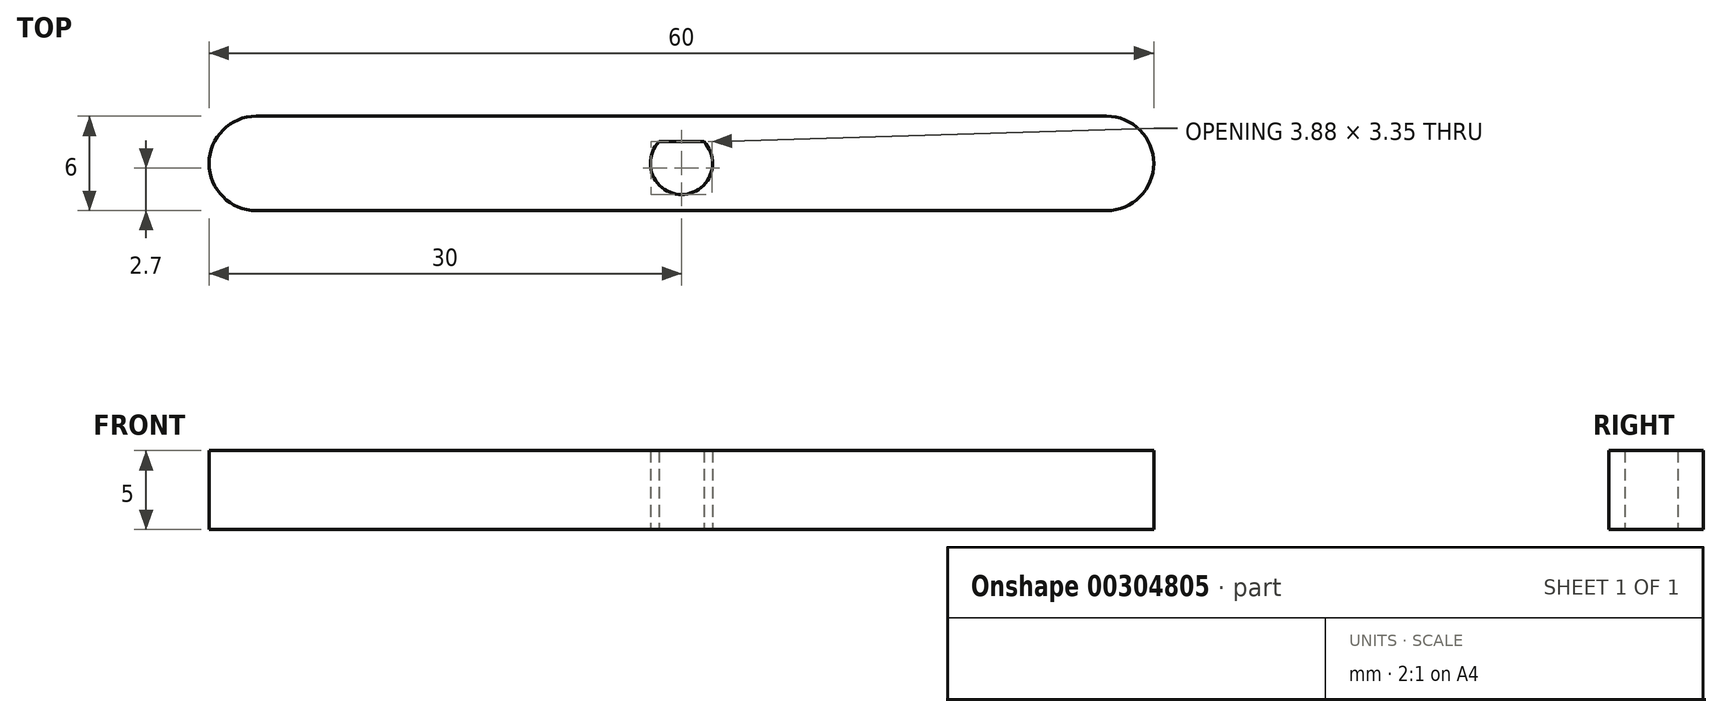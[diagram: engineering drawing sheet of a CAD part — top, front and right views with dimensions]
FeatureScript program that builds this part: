
annotation { "Feature Type Name" : "Feature", "Feature Type Description" : "" }
export const myFeature = defineFeature(function(context is Context, id is Id, definition is map)
    precondition{}
    {
        {
            var Q0;
            Q0=qCreatedBy(makeId("Top.planeOp"),FACE);
            var sketch = newSketch(context, id + "F0", { "sketchPlane" : qUnion([Q0])});
            skLineSegment(sketch, "E0.bottom", {"start": v(27, -3) * mm, "end": v(-27, -3) * mm});
            skLineSegment(sketch, "E0.top", {"start": v(27, 3) * mm, "end": v(-27, 3) * mm});
            skLineSegment(sketch, "E0.left", {"start": v(30, 0) * mm, "end": v(30, 0) * mm});
            skLineSegment(sketch, "E0.right", {"start": v(-30, 0) * mm, "end": v(-30, 0) * mm});
            skPoint(sketch, "E1.visualSharp", {"position": v(-30, 3) * mm});
            skArc(sketch, "E1.filletArc", {"start": v(-27, 3) * mm, "mid": v(-29.12, 2.12) * mm, "end": v(-30, 0) * mm});
            skPoint(sketch, "E2.visualSharp", {"position": v(-30, -3) * mm});
            skArc(sketch, "E2.filletArc", {"start": v(-30, 0) * mm, "mid": v(-29.12, -2.12) * mm, "end": v(-27, -3) * mm});
            skPoint(sketch, "E3.visualSharp", {"position": v(30, -3) * mm});
            skArc(sketch, "E3.filletArc", {"start": v(27, -3) * mm, "mid": v(29.12, -2.12) * mm, "end": v(30, 0) * mm});
            skPoint(sketch, "E4.visualSharp", {"position": v(30, 3) * mm});
            skArc(sketch, "E4.filletArc", {"start": v(30, 0) * mm, "mid": v(29.12, 2.12) * mm, "end": v(27, 3) * mm});
            skPoint(sketch, "E5", {"position": v(0, 0) * mm});
            skArc(sketch, "E6", {"start": v(-1.42, 1.37) * mm, "mid": v(0, -1.98) * mm, "end": v(1.42, 1.37) * mm});
            skLineSegment(sketch, "E7", {"start": v(-1.42, 1.38) * mm, "end": v(1.42, 1.38) * mm});
            skSolve(sketch);
        }
        {
            var Q0;
            Q0=makeQuery(id+"F0.imprint","IMPRINT",FACE,{"disambiguationData":[TD([[makeQuery(id+"F0.imprint","IMPRINT",EDGE,{"derivedFrom":sQuery(id+"F0.wireOp",EDGE,"E0.bottom")}),-1.0]])]});
            extrude(context, id + "F1", {"entities" : qUnion([Q0]), "depth" : 5 * mm});
        }
    });
